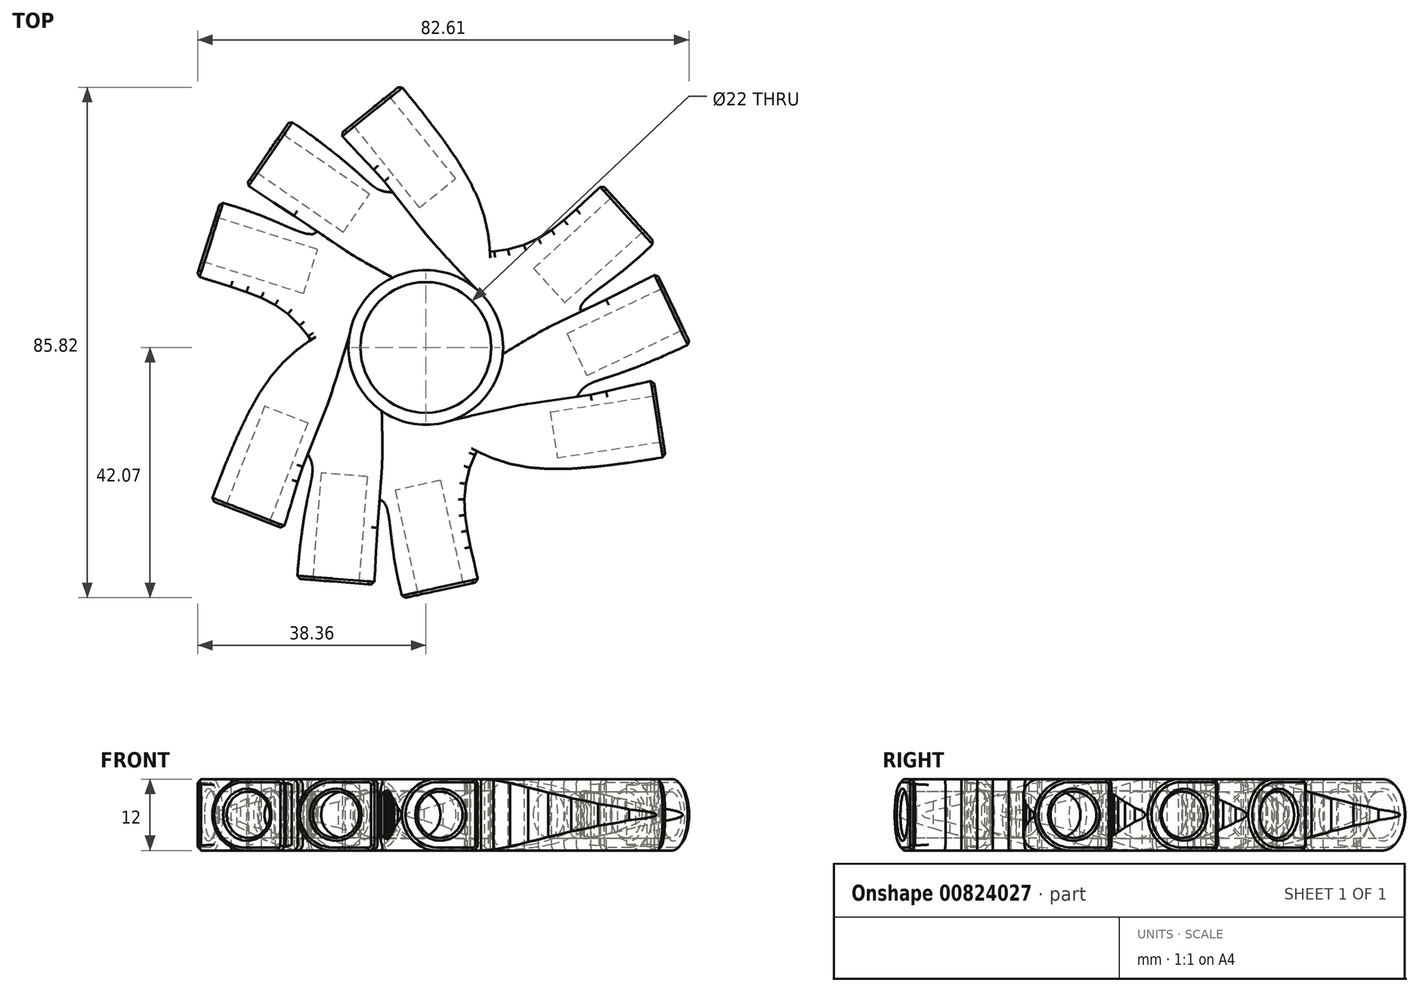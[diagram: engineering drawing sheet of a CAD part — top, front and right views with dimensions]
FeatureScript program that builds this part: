
annotation { "Feature Type Name" : "Feature", "Feature Type Description" : "" }
export const myFeature = defineFeature(function(context is Context, id is Id, definition is map)
    precondition{}
    {
        {
            var Q0;
            Q0=qCreatedBy(makeId("Top.planeOp"),FACE);
            var sketch = newSketch(context, id + "F0", { "sketchPlane" : qUnion([Q0])});
            skLineSegment(sketch, "E0", {"start": v(-3.87, -42.17) * mm, "end": v(8.83, -39.4) * mm});
            skLineSegment(sketch, "E1", {"start": v(8.83, -39.4) * mm, "end": v(8.67, -38.64) * mm});
            skLineSegment(sketch, "E2", {"start": v(8.67, -38.64) * mm, "end": v(8.17, -36.4) * mm});
            skLineSegment(sketch, "E3", {"start": v(8.17, -36.4) * mm, "end": v(7.52, -33.55) * mm});
            skLineSegment(sketch, "E4", {"start": v(7.52, -33.55) * mm, "end": v(6.96, -30.83) * mm});
            skLineSegment(sketch, "E5", {"start": v(6.96, -30.83) * mm, "end": v(6.6, -28.19) * mm});
            skLineSegment(sketch, "E6", {"start": v(6.6, -28.19) * mm, "end": v(6.48, -25.57) * mm});
            skLineSegment(sketch, "E7", {"start": v(6.48, -25.57) * mm, "end": v(6.72, -22.93) * mm});
            skLineSegment(sketch, "E8", {"start": v(6.72, -22.93) * mm, "end": v(7.4, -20.23) * mm});
            skLineSegment(sketch, "E9", {"start": v(7.4, -20.23) * mm, "end": v(8.24, -18.1) * mm});
            skLineSegment(sketch, "E10", {"start": v(8.24, -18.1) * mm, "end": v(8.6, -17.42) * mm});
            skLineSegment(sketch, "E11", {"start": v(8.6, -17.42) * mm, "end": v(9.26, -17.76) * mm});
            skLineSegment(sketch, "E12", {"start": v(9.26, -17.76) * mm, "end": v(11.34, -18.65) * mm});
            skLineSegment(sketch, "E13", {"start": v(11.34, -18.65) * mm, "end": v(14.16, -19.56) * mm});
            skLineSegment(sketch, "E14", {"start": v(14.16, -19.56) * mm, "end": v(17.2, -20.15) * mm});
            skLineSegment(sketch, "E15", {"start": v(17.2, -20.15) * mm, "end": v(20.6, -20.42) * mm});
            skLineSegment(sketch, "E16", {"start": v(20.6, -20.42) * mm, "end": v(24.46, -20.37) * mm});
            skLineSegment(sketch, "E17", {"start": v(24.46, -20.37) * mm, "end": v(28.95, -20.02) * mm});
            skLineSegment(sketch, "E18", {"start": v(28.95, -20.02) * mm, "end": v(34.19, -19.35) * mm});
            skLineSegment(sketch, "E19", {"start": v(34.19, -19.35) * mm, "end": v(38.78, -18.65) * mm});
            skLineSegment(sketch, "E20", {"start": v(38.78, -18.65) * mm, "end": v(40.3, -18.39) * mm});
            skLineSegment(sketch, "E21", {"start": v(40.3, -18.39) * mm, "end": v(38.33, -5.54) * mm});
            skLineSegment(sketch, "E22", {"start": v(38.33, -5.54) * mm, "end": v(37.16, -5.78) * mm});
            skLineSegment(sketch, "E23", {"start": v(37.16, -5.78) * mm, "end": v(33.7, -6.57) * mm});
            skLineSegment(sketch, "E24", {"start": v(33.7, -6.57) * mm, "end": v(30.3, -7.38) * mm});
            skLineSegment(sketch, "E25", {"start": v(30.3, -7.38) * mm, "end": v(27.7, -7.94) * mm});
            skLineSegment(sketch, "E26", {"start": v(27.7, -7.94) * mm, "end": v(26.02, -8.19) * mm});
            skLineSegment(sketch, "E27", {"start": v(26.02, -8.19) * mm, "end": v(25.45, -8.22) * mm});
            skLineSegment(sketch, "E28", {"start": v(25.45, -8.22) * mm, "end": v(25.62, -7.92) * mm});
            skLineSegment(sketch, "E29", {"start": v(25.62, -7.92) * mm, "end": v(26.22, -7.09) * mm});
            skLineSegment(sketch, "E30", {"start": v(26.22, -7.09) * mm, "end": v(27.1, -6.34) * mm});
            skLineSegment(sketch, "E31", {"start": v(27.1, -6.34) * mm, "end": v(28.29, -5.78) * mm});
            skLineSegment(sketch, "E32", {"start": v(28.29, -5.78) * mm, "end": v(29.92, -5.22) * mm});
            skLineSegment(sketch, "E33", {"start": v(29.92, -5.22) * mm, "end": v(32.2, -4.48) * mm});
            skLineSegment(sketch, "E34", {"start": v(32.2, -4.48) * mm, "end": v(35.26, -3.38) * mm});
            skLineSegment(sketch, "E35", {"start": v(35.26, -3.38) * mm, "end": v(39.3, -1.73) * mm});
            skLineSegment(sketch, "E36", {"start": v(39.3, -1.73) * mm, "end": v(43.18, 0.04) * mm});
            skLineSegment(sketch, "E37", {"start": v(43.18, 0.04) * mm, "end": v(44.46, 0.66) * mm});
            skLineSegment(sketch, "E38", {"start": v(44.46, 0.66) * mm, "end": v(38.88, 12.4) * mm});
            skLineSegment(sketch, "E39", {"start": v(38.88, 12.4) * mm, "end": v(37.64, 11.78) * mm});
            skLineSegment(sketch, "E40", {"start": v(37.64, 11.78) * mm, "end": v(33.94, 9.92) * mm});
            skLineSegment(sketch, "E41", {"start": v(33.94, 9.92) * mm, "end": v(30.3, 8.08) * mm});
            skLineSegment(sketch, "E42", {"start": v(30.3, 8.08) * mm, "end": v(27.73, 6.83) * mm});
            skLineSegment(sketch, "E43", {"start": v(27.73, 6.83) * mm, "end": v(26.49, 6.28) * mm});
            skLineSegment(sketch, "E44", {"start": v(26.49, 6.28) * mm, "end": v(26.06, 6.14) * mm});
            skLineSegment(sketch, "E45", {"start": v(26.06, 6.14) * mm, "end": v(25.98, 6.3) * mm});
            skLineSegment(sketch, "E46", {"start": v(25.98, 6.3) * mm, "end": v(26.03, 6.93) * mm});
            skLineSegment(sketch, "E47", {"start": v(26.03, 6.93) * mm, "end": v(26.62, 7.8) * mm});
            skLineSegment(sketch, "E48", {"start": v(26.62, 7.8) * mm, "end": v(27.73, 8.8) * mm});
            skLineSegment(sketch, "E49", {"start": v(27.73, 8.8) * mm, "end": v(29.3, 10) * mm});
            skLineSegment(sketch, "E50", {"start": v(29.3, 10) * mm, "end": v(31.24, 11.44) * mm});
            skLineSegment(sketch, "E51", {"start": v(31.24, 11.44) * mm, "end": v(33.46, 13.17) * mm});
            skLineSegment(sketch, "E52", {"start": v(33.46, 13.17) * mm, "end": v(35.89, 15.24) * mm});
            skLineSegment(sketch, "E53", {"start": v(35.89, 15.24) * mm, "end": v(37.83, 17.06) * mm});
            skLineSegment(sketch, "E54", {"start": v(37.83, 17.06) * mm, "end": v(38.44, 17.7) * mm});
            skLineSegment(sketch, "E55", {"start": v(38.44, 17.7) * mm, "end": v(29.69, 27.3) * mm});
            skLineSegment(sketch, "E56", {"start": v(29.69, 27.3) * mm, "end": v(29.11, 26.8) * mm});
            skLineSegment(sketch, "E57", {"start": v(29.11, 26.8) * mm, "end": v(27.42, 25.23) * mm});
            skLineSegment(sketch, "E58", {"start": v(27.42, 25.23) * mm, "end": v(25.28, 23.25) * mm});
            skLineSegment(sketch, "E59", {"start": v(25.28, 23.25) * mm, "end": v(23.2, 21.41) * mm});
            skLineSegment(sketch, "E60", {"start": v(23.2, 21.41) * mm, "end": v(21.1, 19.77) * mm});
            skLineSegment(sketch, "E61", {"start": v(21.1, 19.77) * mm, "end": v(18.89, 18.37) * mm});
            skLineSegment(sketch, "E62", {"start": v(18.89, 18.37) * mm, "end": v(16.48, 17.26) * mm});
            skLineSegment(sketch, "E63", {"start": v(16.48, 17.26) * mm, "end": v(13.8, 16.5) * mm});
            skLineSegment(sketch, "E64", {"start": v(13.8, 16.5) * mm, "end": v(11.53, 16.15) * mm});
            skLineSegment(sketch, "E65", {"start": v(11.53, 16.15) * mm, "end": v(10.77, 16.12) * mm});
            skLineSegment(sketch, "E66", {"start": v(10.77, 16.12) * mm, "end": v(10.73, 16.87) * mm});
            skLineSegment(sketch, "E67", {"start": v(10.73, 16.87) * mm, "end": v(10.47, 19.11) * mm});
            skLineSegment(sketch, "E68", {"start": v(10.47, 19.11) * mm, "end": v(9.84, 22.01) * mm});
            skLineSegment(sketch, "E69", {"start": v(9.84, 22.01) * mm, "end": v(8.83, 24.94) * mm});
            skLineSegment(sketch, "E70", {"start": v(8.83, 24.94) * mm, "end": v(7.37, 28) * mm});
            skLineSegment(sketch, "E71", {"start": v(7.37, 28) * mm, "end": v(5.4, 31.34) * mm});
            skLineSegment(sketch, "E72", {"start": v(5.4, 31.34) * mm, "end": v(2.84, 35.05) * mm});
            skLineSegment(sketch, "E73", {"start": v(2.84, 35.05) * mm, "end": v(-0.35, 39.25) * mm});
            skLineSegment(sketch, "E74", {"start": v(-0.35, 39.25) * mm, "end": v(-3.26, 42.87) * mm});
            skLineSegment(sketch, "E75", {"start": v(-3.26, 42.87) * mm, "end": v(-4.24, 44.06) * mm});
            skLineSegment(sketch, "E76", {"start": v(-4.24, 44.06) * mm, "end": v(-14.38, 35.92) * mm});
            skLineSegment(sketch, "E77", {"start": v(-14.38, 35.92) * mm, "end": v(-13.6, 35.04) * mm});
            skLineSegment(sketch, "E78", {"start": v(-13.6, 35.04) * mm, "end": v(-11.17, 32.43) * mm});
            skLineSegment(sketch, "E79", {"start": v(-11.17, 32.43) * mm, "end": v(-8.77, 29.9) * mm});
            skLineSegment(sketch, "E80", {"start": v(-8.77, 29.9) * mm, "end": v(-7, 27.93) * mm});
            skLineSegment(sketch, "E81", {"start": v(-7, 27.93) * mm, "end": v(-5.94, 26.59) * mm});
            skLineSegment(sketch, "E82", {"start": v(-5.94, 26.59) * mm, "end": v(-5.63, 26.11) * mm});
            skLineSegment(sketch, "E83", {"start": v(-5.63, 26.11) * mm, "end": v(-5.97, 26.1) * mm});
            skLineSegment(sketch, "E84", {"start": v(-5.97, 26.1) * mm, "end": v(-6.99, 26.21) * mm});
            skLineSegment(sketch, "E85", {"start": v(-6.99, 26.21) * mm, "end": v(-8.08, 26.6) * mm});
            skLineSegment(sketch, "E86", {"start": v(-8.08, 26.6) * mm, "end": v(-9.16, 27.35) * mm});
            skLineSegment(sketch, "E87", {"start": v(-9.16, 27.35) * mm, "end": v(-10.46, 28.5) * mm});
            skLineSegment(sketch, "E88", {"start": v(-10.46, 28.5) * mm, "end": v(-12.23, 30.09) * mm});
            skLineSegment(sketch, "E89", {"start": v(-12.23, 30.09) * mm, "end": v(-14.72, 32.2) * mm});
            skLineSegment(sketch, "E90", {"start": v(-14.72, 32.2) * mm, "end": v(-18.17, 34.86) * mm});
            skLineSegment(sketch, "E91", {"start": v(-18.17, 34.86) * mm, "end": v(-21.64, 37.35) * mm});
            skLineSegment(sketch, "E92", {"start": v(-21.64, 37.35) * mm, "end": v(-22.82, 38.14) * mm});
            skLineSegment(sketch, "E93", {"start": v(-22.82, 38.14) * mm, "end": v(-30.2, 27.43) * mm});
            skLineSegment(sketch, "E94", {"start": v(-30.2, 27.43) * mm, "end": v(-29.04, 26.67) * mm});
            skLineSegment(sketch, "E95", {"start": v(-29.04, 26.67) * mm, "end": v(-25.58, 24.4) * mm});
            skLineSegment(sketch, "E96", {"start": v(-25.58, 24.4) * mm, "end": v(-22.16, 22.16) * mm});
            skLineSegment(sketch, "E97", {"start": v(-22.16, 22.16) * mm, "end": v(-19.8, 20.56) * mm});
            skLineSegment(sketch, "E98", {"start": v(-19.8, 20.56) * mm, "end": v(-18.7, 19.76) * mm});
            skLineSegment(sketch, "E99", {"start": v(-18.7, 19.76) * mm, "end": v(-18.36, 19.46) * mm});
            skLineSegment(sketch, "E100", {"start": v(-18.36, 19.46) * mm, "end": v(-18.46, 19.31) * mm});
            skLineSegment(sketch, "E101", {"start": v(-18.46, 19.31) * mm, "end": v(-19.03, 19.04) * mm});
            skLineSegment(sketch, "E102", {"start": v(-19.03, 19.04) * mm, "end": v(-20.08, 19.11) * mm});
            skLineSegment(sketch, "E103", {"start": v(-20.08, 19.11) * mm, "end": v(-21.51, 19.58) * mm});
            skLineSegment(sketch, "E104", {"start": v(-21.51, 19.58) * mm, "end": v(-23.33, 20.34) * mm});
            skLineSegment(sketch, "E105", {"start": v(-23.33, 20.34) * mm, "end": v(-25.54, 21.3) * mm});
            skLineSegment(sketch, "E106", {"start": v(-25.54, 21.3) * mm, "end": v(-28.15, 22.36) * mm});
            skLineSegment(sketch, "E107", {"start": v(-28.15, 22.36) * mm, "end": v(-31.16, 23.43) * mm});
            skLineSegment(sketch, "E108", {"start": v(-31.16, 23.43) * mm, "end": v(-33.7, 24.2) * mm});
            skLineSegment(sketch, "E109", {"start": v(-33.7, 24.2) * mm, "end": v(-34.56, 24.4) * mm});
            skLineSegment(sketch, "E110", {"start": v(-34.56, 24.4) * mm, "end": v(-38.5, 12.02) * mm});
            skLineSegment(sketch, "E111", {"start": v(-38.5, 12.02) * mm, "end": v(-37.78, 11.78) * mm});
            skLineSegment(sketch, "E112", {"start": v(-37.78, 11.78) * mm, "end": v(-35.58, 11.1) * mm});
            skLineSegment(sketch, "E113", {"start": v(-35.58, 11.1) * mm, "end": v(-32.8, 10.23) * mm});
            skLineSegment(sketch, "E114", {"start": v(-32.8, 10.23) * mm, "end": v(-30.16, 9.35) * mm});
            skLineSegment(sketch, "E115", {"start": v(-30.16, 9.35) * mm, "end": v(-27.69, 8.35) * mm});
            skLineSegment(sketch, "E116", {"start": v(-27.69, 8.35) * mm, "end": v(-25.36, 7.14) * mm});
            skLineSegment(sketch, "E117", {"start": v(-25.36, 7.14) * mm, "end": v(-23.2, 5.61) * mm});
            skLineSegment(sketch, "E118", {"start": v(-23.2, 5.61) * mm, "end": v(-21.2, 3.68) * mm});
            skLineSegment(sketch, "E119", {"start": v(-21.2, 3.68) * mm, "end": v(-19.77, 1.88) * mm});
            skLineSegment(sketch, "E120", {"start": v(-19.77, 1.88) * mm, "end": v(-19.36, 1.24) * mm});
            skLineSegment(sketch, "E121", {"start": v(-19.36, 1.24) * mm, "end": v(-20, 0.83) * mm});
            skLineSegment(sketch, "E122", {"start": v(-20, 0.83) * mm, "end": v(-21.8, -0.52) * mm});
            skLineSegment(sketch, "E123", {"start": v(-21.8, -0.52) * mm, "end": v(-24, -2.52) * mm});
            skLineSegment(sketch, "E124", {"start": v(-24, -2.52) * mm, "end": v(-26.03, -4.86) * mm});
            skLineSegment(sketch, "E125", {"start": v(-26.03, -4.86) * mm, "end": v(-27.96, -7.66) * mm});
            skLineSegment(sketch, "E126", {"start": v(-27.96, -7.66) * mm, "end": v(-29.85, -11.03) * mm});
            skLineSegment(sketch, "E127", {"start": v(-29.85, -11.03) * mm, "end": v(-31.79, -15.1) * mm});
            skLineSegment(sketch, "E128", {"start": v(-31.79, -15.1) * mm, "end": v(-33.83, -19.96) * mm});
            skLineSegment(sketch, "E129", {"start": v(-33.83, -19.96) * mm, "end": v(-35.51, -24.3) * mm});
            skLineSegment(sketch, "E130", {"start": v(-35.51, -24.3) * mm, "end": v(-36.05, -25.74) * mm});
            skLineSegment(sketch, "E131", {"start": v(-36.05, -25.74) * mm, "end": v(-23.94, -30.45) * mm});
            skLineSegment(sketch, "E132", {"start": v(-23.94, -30.45) * mm, "end": v(-23.57, -29.33) * mm});
            skLineSegment(sketch, "E133", {"start": v(-23.57, -29.33) * mm, "end": v(-22.52, -25.92) * mm});
            skLineSegment(sketch, "E134", {"start": v(-22.52, -25.92) * mm, "end": v(-21.52, -22.58) * mm});
            skLineSegment(sketch, "E135", {"start": v(-21.52, -22.58) * mm, "end": v(-20.7, -20.06) * mm});
            skLineSegment(sketch, "E136", {"start": v(-20.7, -20.06) * mm, "end": v(-20.07, -18.47) * mm});
            skLineSegment(sketch, "E137", {"start": v(-20.07, -18.47) * mm, "end": v(-19.82, -17.97) * mm});
            skLineSegment(sketch, "E138", {"start": v(-19.82, -17.97) * mm, "end": v(-19.64, -18.26) * mm});
            skLineSegment(sketch, "E139", {"start": v(-19.64, -18.26) * mm, "end": v(-19.23, -19.2) * mm});
            skLineSegment(sketch, "E140", {"start": v(-19.23, -19.2) * mm, "end": v(-19.02, -20.34) * mm});
            skLineSegment(sketch, "E141", {"start": v(-19.02, -20.34) * mm, "end": v(-19.12, -21.64) * mm});
            skLineSegment(sketch, "E142", {"start": v(-19.12, -21.64) * mm, "end": v(-19.46, -23.34) * mm});
            skLineSegment(sketch, "E143", {"start": v(-19.46, -23.34) * mm, "end": v(-19.96, -25.67) * mm});
            skLineSegment(sketch, "E144", {"start": v(-19.96, -25.67) * mm, "end": v(-20.53, -28.88) * mm});
            skLineSegment(sketch, "E145", {"start": v(-20.53, -28.88) * mm, "end": v(-21.12, -33.2) * mm});
            skLineSegment(sketch, "E146", {"start": v(-21.12, -33.2) * mm, "end": v(-21.54, -37.45) * mm});
            skLineSegment(sketch, "E147", {"start": v(-21.54, -37.45) * mm, "end": v(-21.64, -38.87) * mm});
            skLineSegment(sketch, "E148", {"start": v(-21.64, -38.87) * mm, "end": v(-8.68, -39.9) * mm});
            skLineSegment(sketch, "E149", {"start": v(-8.68, -39.9) * mm, "end": v(-8.6, -38.52) * mm});
            skLineSegment(sketch, "E150", {"start": v(-8.6, -38.52) * mm, "end": v(-8.36, -34.39) * mm});
            skLineSegment(sketch, "E151", {"start": v(-8.36, -34.39) * mm, "end": v(-8.13, -30.3) * mm});
            skLineSegment(sketch, "E152", {"start": v(-8.13, -30.3) * mm, "end": v(-7.92, -27.46) * mm});
            skLineSegment(sketch, "E153", {"start": v(-7.92, -27.46) * mm, "end": v(-7.78, -26.11) * mm});
            skLineSegment(sketch, "E154", {"start": v(-7.78, -26.11) * mm, "end": v(-7.69, -25.67) * mm});
            skLineSegment(sketch, "E155", {"start": v(-7.69, -25.67) * mm, "end": v(-7.51, -25.68) * mm});
            skLineSegment(sketch, "E156", {"start": v(-7.51, -25.68) * mm, "end": v(-7, -26.04) * mm});
            skLineSegment(sketch, "E157", {"start": v(-7, -26.04) * mm, "end": v(-6.53, -26.98) * mm});
            skLineSegment(sketch, "E158", {"start": v(-6.53, -26.98) * mm, "end": v(-6.22, -28.45) * mm});
            skLineSegment(sketch, "E159", {"start": v(-6.22, -28.45) * mm, "end": v(-5.96, -30.41) * mm});
            skLineSegment(sketch, "E160", {"start": v(-5.96, -30.41) * mm, "end": v(-5.69, -32.8) * mm});
            skLineSegment(sketch, "E161", {"start": v(-5.69, -32.8) * mm, "end": v(-5.3, -35.6) * mm});
            skLineSegment(sketch, "E162", {"start": v(-5.3, -35.6) * mm, "end": v(-4.73, -38.73) * mm});
            skLineSegment(sketch, "E163", {"start": v(-4.73, -38.73) * mm, "end": v(-4.12, -41.32) * mm});
            skLineSegment(sketch, "E164", {"start": v(-4.12, -41.32) * mm, "end": v(-3.87, -42.17) * mm});
            skCircle(sketch, "E165", {"center": v(0, 0) * mm, "radius": 11 * mm});
            skSolve(sketch);
        }
        {
            var Q0;
            Q0=makeQuery(id+"F0.imprint","IMPRINT",FACE,{"disambiguationData":[TD([[makeQuery(id+"F0.imprint","IMPRINT",EDGE,{"derivedFrom":sQuery(id+"F0.wireOp",EDGE,"E0")}),1.0]])]});
            extrude(context, id + "F1", {"entities" : qUnion([Q0]), "endBound" : BoundingType.SYMMETRIC, "depth" : 12 * mm, "offsetDistance" : 25 * mm});
        }
        {
            var Q0;
            Q0=makeQuery(id+"F1.opExtrude","CAP_EDGE",EDGE,{"disambiguationData":[OSD([sQuery(id+"F0.wireOp",EDGE,"E130")])],"isStart":false});
            var Q1;
            Q1=makeQuery(id+"F1.opExtrude","CAP_EDGE",EDGE,{"disambiguationData":[OSD([sQuery(id+"F0.wireOp",EDGE,"E147")])],"isStart":false});
            var Q2;
            Q2=makeQuery(id+"F1.opExtrude","CAP_EDGE",EDGE,{"disambiguationData":[OSD([sQuery(id+"F0.wireOp",EDGE,"E164")])],"isStart":false});
            var Q3;
            Q3=makeQuery(id+"F1.opExtrude","CAP_EDGE",EDGE,{"disambiguationData":[OSD([sQuery(id+"F0.wireOp",EDGE,"E20")])],"isStart":false});
            var Q4;
            Q4=makeQuery(id+"F1.opExtrude","CAP_EDGE",EDGE,{"disambiguationData":[OSD([sQuery(id+"F0.wireOp",EDGE,"E37")])],"isStart":false});
            var Q5;
            Q5=makeQuery(id+"F1.opExtrude","CAP_EDGE",EDGE,{"disambiguationData":[OSD([sQuery(id+"F0.wireOp",EDGE,"E54")])],"isStart":false});
            var Q6;
            Q6=makeQuery(id+"F1.opExtrude","CAP_EDGE",EDGE,{"disambiguationData":[OSD([sQuery(id+"F0.wireOp",EDGE,"E75")])],"isStart":false});
            var Q7;
            Q7=makeQuery(id+"F1.opExtrude","CAP_EDGE",EDGE,{"disambiguationData":[OSD([sQuery(id+"F0.wireOp",EDGE,"E92")])],"isStart":false});
            var Q8;
            Q8=makeQuery(id+"F1.opExtrude","CAP_EDGE",EDGE,{"disambiguationData":[OSD([sQuery(id+"F0.wireOp",EDGE,"E109")])],"isStart":false});
            fillet(context, id + "F2", {"entities" : qUnion([Q0, Q1, Q2, Q3, Q4, Q5, Q6, Q7, Q8]), "radius" : 6 * mm, "tangentPropagation" : true, "allowEdgeOverflow" : false});
        }
        {
            var Q0;
            Q0=makeQuery(id+"F1.opExtrude","CAP_EDGE",EDGE,{"disambiguationData":[OSD([sQuery(id+"F0.wireOp",EDGE,"E147")])],"isStart":true});
            var Q1;
            Q1=makeQuery(id+"F1.opExtrude","CAP_EDGE",EDGE,{"disambiguationData":[OSD([sQuery(id+"F0.wireOp",EDGE,"E130")])],"isStart":true});
            var Q2;
            Q2=makeQuery(id+"F1.opExtrude","CAP_EDGE",EDGE,{"disambiguationData":[OSD([sQuery(id+"F0.wireOp",EDGE,"E164")])],"isStart":true});
            var Q3;
            Q3=makeQuery(id+"F1.opExtrude","CAP_EDGE",EDGE,{"disambiguationData":[OSD([sQuery(id+"F0.wireOp",EDGE,"E20")])],"isStart":true});
            var Q4;
            Q4=makeQuery(id+"F1.opExtrude","CAP_EDGE",EDGE,{"disambiguationData":[OSD([sQuery(id+"F0.wireOp",EDGE,"E37")])],"isStart":true});
            var Q5;
            Q5=makeQuery(id+"F1.opExtrude","CAP_EDGE",EDGE,{"disambiguationData":[OSD([sQuery(id+"F0.wireOp",EDGE,"E54")])],"isStart":true});
            var Q6;
            Q6=makeQuery(id+"F1.opExtrude","CAP_EDGE",EDGE,{"disambiguationData":[OSD([sQuery(id+"F0.wireOp",EDGE,"E75")])],"isStart":true});
            var Q7;
            Q7=makeQuery(id+"F1.opExtrude","CAP_EDGE",EDGE,{"disambiguationData":[OSD([sQuery(id+"F0.wireOp",EDGE,"E92")])],"isStart":true});
            var Q8;
            Q8=makeQuery(id+"F1.opExtrude","CAP_EDGE",EDGE,{"disambiguationData":[OSD([sQuery(id+"F0.wireOp",EDGE,"E109")])],"isStart":true});
            fillet(context, id + "F3", {"entities" : qUnion([Q0, Q1, Q2, Q3, Q4, Q5, Q6, Q7, Q8]), "radius" : 6 * mm, "tangentPropagation" : true, "allowEdgeOverflow" : false});
        }
        {
            var Q0;
            Q0=makeQuery(id+"F1.opExtrude","CAP_EDGE",EDGE,{"disambiguationData":[OSD([sQuery(id+"F0.wireOp",EDGE,"E165")])],"isStart":false});
            chamfer(context, id + "F4", {"entities" : qUnion([Q0]), "width" : 2 * mm, "tangentPropagation" : true});
        }
        {
            var Q0;
            Q0=makeQuery(id+"F1.opExtrude","CAP_EDGE",EDGE,{"disambiguationData":[OSD([sQuery(id+"F0.wireOp",EDGE,"E165")])],"isStart":true});
            chamfer(context, id + "F5", {"entities" : qUnion([Q0]), "width" : 2 * mm, "tangentPropagation" : true});
        }
        {
            var Q0;
            Q0=makeQuery(id+"F1.opExtrude","CAP_EDGE",EDGE,{"disambiguationData":[OSD([sQuery(id+"F0.wireOp",EDGE,"E136")])],"isStart":false});
            var Q1;
            Q1=makeQuery(id+"F1.opExtrude","CAP_EDGE",EDGE,{"disambiguationData":[OSD([sQuery(id+"F0.wireOp",EDGE,"E135")])],"isStart":false});
            var Q2;
            Q2=makeQuery(id+"F1.opExtrude","CAP_EDGE",EDGE,{"disambiguationData":[OSD([sQuery(id+"F0.wireOp",EDGE,"E152")])],"isStart":false});
            var Q3;
            Q3=makeQuery(id+"F1.opExtrude","CAP_EDGE",EDGE,{"disambiguationData":[OSD([sQuery(id+"F0.wireOp",EDGE,"E10")])],"isStart":false});
            var Q4;
            Q4=makeQuery(id+"F1.opExtrude","CAP_EDGE",EDGE,{"disambiguationData":[OSD([sQuery(id+"F0.wireOp",EDGE,"E8")])],"isStart":false});
            var Q5;
            Q5=makeQuery(id+"F1.opExtrude","CAP_EDGE",EDGE,{"disambiguationData":[OSD([sQuery(id+"F0.wireOp",EDGE,"E9")])],"isStart":false});
            var Q6;
            Q6=makeQuery(id+"F1.opExtrude","CAP_EDGE",EDGE,{"disambiguationData":[OSD([sQuery(id+"F0.wireOp",EDGE,"E7")])],"isStart":false});
            var Q7;
            Q7=makeQuery(id+"F1.opExtrude","CAP_EDGE",EDGE,{"disambiguationData":[OSD([sQuery(id+"F0.wireOp",EDGE,"E6")])],"isStart":false});
            var Q8;
            Q8=makeQuery(id+"F1.opExtrude","CAP_EDGE",EDGE,{"disambiguationData":[OSD([sQuery(id+"F0.wireOp",EDGE,"E5")])],"isStart":false});
            var Q9;
            Q9=makeQuery(id+"F1.opExtrude","CAP_EDGE",EDGE,{"disambiguationData":[OSD([sQuery(id+"F0.wireOp",EDGE,"E4")])],"isStart":false});
            var Q10;
            Q10=makeQuery(id+"F1.opExtrude","CAP_EDGE",EDGE,{"disambiguationData":[OSD([sQuery(id+"F0.wireOp",EDGE,"E26")])],"isStart":false});
            var Q11;
            Q11=makeQuery(id+"F1.opExtrude","CAP_EDGE",EDGE,{"disambiguationData":[OSD([sQuery(id+"F0.wireOp",EDGE,"E25")])],"isStart":false});
            var Q12;
            Q12=makeQuery(id+"F1.opExtrude","CAP_EDGE",EDGE,{"disambiguationData":[OSD([sQuery(id+"F0.wireOp",EDGE,"E42")])],"isStart":false});
            var Q13;
            Q13=makeQuery(id+"F1.opExtrude","CAP_EDGE",EDGE,{"disambiguationData":[OSD([sQuery(id+"F0.wireOp",EDGE,"E65")])],"isStart":false});
            var Q14;
            Q14=makeQuery(id+"F1.opExtrude","CAP_EDGE",EDGE,{"disambiguationData":[OSD([sQuery(id+"F0.wireOp",EDGE,"E64")])],"isStart":false});
            var Q15;
            Q15=makeQuery(id+"F1.opExtrude","CAP_EDGE",EDGE,{"disambiguationData":[OSD([sQuery(id+"F0.wireOp",EDGE,"E63")])],"isStart":false});
            var Q16;
            Q16=makeQuery(id+"F1.opExtrude","CAP_EDGE",EDGE,{"disambiguationData":[OSD([sQuery(id+"F0.wireOp",EDGE,"E62")])],"isStart":false});
            var Q17;
            Q17=makeQuery(id+"F1.opExtrude","CAP_EDGE",EDGE,{"disambiguationData":[OSD([sQuery(id+"F0.wireOp",EDGE,"E61")])],"isStart":false});
            var Q18;
            Q18=makeQuery(id+"F1.opExtrude","CAP_EDGE",EDGE,{"disambiguationData":[OSD([sQuery(id+"F0.wireOp",EDGE,"E60")])],"isStart":false});
            var Q19;
            Q19=makeQuery(id+"F1.opExtrude","CAP_EDGE",EDGE,{"disambiguationData":[OSD([sQuery(id+"F0.wireOp",EDGE,"E81")])],"isStart":false});
            var Q20;
            Q20=makeQuery(id+"F1.opExtrude","CAP_EDGE",EDGE,{"disambiguationData":[OSD([sQuery(id+"F0.wireOp",EDGE,"E97")])],"isStart":false});
            var Q21;
            Q21=makeQuery(id+"F1.opExtrude","CAP_EDGE",EDGE,{"disambiguationData":[OSD([sQuery(id+"F0.wireOp",EDGE,"E80")])],"isStart":false});
            var Q22;
            Q22=makeQuery(id+"F1.opExtrude","CAP_EDGE",EDGE,{"disambiguationData":[OSD([sQuery(id+"F0.wireOp",EDGE,"E120")])],"isStart":false});
            var Q23;
            Q23=makeQuery(id+"F1.opExtrude","CAP_EDGE",EDGE,{"disambiguationData":[OSD([sQuery(id+"F0.wireOp",EDGE,"E119")])],"isStart":false});
            var Q24;
            Q24=makeQuery(id+"F1.opExtrude","CAP_EDGE",EDGE,{"disambiguationData":[OSD([sQuery(id+"F0.wireOp",EDGE,"E118")])],"isStart":false});
            var Q25;
            Q25=makeQuery(id+"F1.opExtrude","CAP_EDGE",EDGE,{"disambiguationData":[OSD([sQuery(id+"F0.wireOp",EDGE,"E117")])],"isStart":false});
            var Q26;
            Q26=makeQuery(id+"F1.opExtrude","CAP_EDGE",EDGE,{"disambiguationData":[OSD([sQuery(id+"F0.wireOp",EDGE,"E116")])],"isStart":false});
            var Q27;
            Q27=makeQuery(id+"F1.opExtrude","CAP_EDGE",EDGE,{"disambiguationData":[OSD([sQuery(id+"F0.wireOp",EDGE,"E115")])],"isStart":false});
            var Q28;
            Q28=makeQuery(id+"F1.opExtrude","CAP_EDGE",EDGE,{"disambiguationData":[OSD([sQuery(id+"F0.wireOp",EDGE,"E114")])],"isStart":false});
            var Q29;
            Q29=makeQuery(id+"F1.opExtrude","CAP_EDGE",EDGE,{"disambiguationData":[OSD([sQuery(id+"F0.wireOp",EDGE,"E136")])],"isStart":true});
            var Q30;
            Q30=makeQuery(id+"F1.opExtrude","CAP_EDGE",EDGE,{"disambiguationData":[OSD([sQuery(id+"F0.wireOp",EDGE,"E135")])],"isStart":true});
            var Q31;
            Q31=makeQuery(id+"F1.opExtrude","CAP_EDGE",EDGE,{"disambiguationData":[OSD([sQuery(id+"F0.wireOp",EDGE,"E152")])],"isStart":true});
            var Q32;
            Q32=makeQuery(id+"F1.opExtrude","CAP_EDGE",EDGE,{"disambiguationData":[OSD([sQuery(id+"F0.wireOp",EDGE,"E10")])],"isStart":true});
            var Q33;
            Q33=makeQuery(id+"F1.opExtrude","CAP_EDGE",EDGE,{"disambiguationData":[OSD([sQuery(id+"F0.wireOp",EDGE,"E9")])],"isStart":true});
            var Q34;
            Q34=makeQuery(id+"F1.opExtrude","CAP_EDGE",EDGE,{"disambiguationData":[OSD([sQuery(id+"F0.wireOp",EDGE,"E8")])],"isStart":true});
            var Q35;
            Q35=makeQuery(id+"F1.opExtrude","CAP_EDGE",EDGE,{"disambiguationData":[OSD([sQuery(id+"F0.wireOp",EDGE,"E7")])],"isStart":true});
            var Q36;
            Q36=makeQuery(id+"F1.opExtrude","CAP_EDGE",EDGE,{"disambiguationData":[OSD([sQuery(id+"F0.wireOp",EDGE,"E6")])],"isStart":true});
            var Q37;
            Q37=makeQuery(id+"F1.opExtrude","CAP_EDGE",EDGE,{"disambiguationData":[OSD([sQuery(id+"F0.wireOp",EDGE,"E5")])],"isStart":true});
            var Q38;
            Q38=makeQuery(id+"F1.opExtrude","CAP_EDGE",EDGE,{"disambiguationData":[OSD([sQuery(id+"F0.wireOp",EDGE,"E4")])],"isStart":true});
            var Q39;
            Q39=makeQuery(id+"F1.opExtrude","CAP_EDGE",EDGE,{"disambiguationData":[OSD([sQuery(id+"F0.wireOp",EDGE,"E26")])],"isStart":true});
            var Q40;
            Q40=makeQuery(id+"F1.opExtrude","CAP_EDGE",EDGE,{"disambiguationData":[OSD([sQuery(id+"F0.wireOp",EDGE,"E25")])],"isStart":true});
            var Q41;
            Q41=makeQuery(id+"F1.opExtrude","CAP_EDGE",EDGE,{"disambiguationData":[OSD([sQuery(id+"F0.wireOp",EDGE,"E42")])],"isStart":true});
            var Q42;
            Q42=makeQuery(id+"F1.opExtrude","CAP_EDGE",EDGE,{"disambiguationData":[OSD([sQuery(id+"F0.wireOp",EDGE,"E65")])],"isStart":true});
            var Q43;
            Q43=makeQuery(id+"F1.opExtrude","CAP_EDGE",EDGE,{"disambiguationData":[OSD([sQuery(id+"F0.wireOp",EDGE,"E64")])],"isStart":true});
            var Q44;
            Q44=makeQuery(id+"F1.opExtrude","CAP_EDGE",EDGE,{"disambiguationData":[OSD([sQuery(id+"F0.wireOp",EDGE,"E63")])],"isStart":true});
            var Q45;
            Q45=makeQuery(id+"F1.opExtrude","CAP_EDGE",EDGE,{"disambiguationData":[OSD([sQuery(id+"F0.wireOp",EDGE,"E62")])],"isStart":true});
            var Q46;
            Q46=makeQuery(id+"F1.opExtrude","CAP_EDGE",EDGE,{"disambiguationData":[OSD([sQuery(id+"F0.wireOp",EDGE,"E61")])],"isStart":true});
            var Q47;
            Q47=makeQuery(id+"F1.opExtrude","CAP_EDGE",EDGE,{"disambiguationData":[OSD([sQuery(id+"F0.wireOp",EDGE,"E60")])],"isStart":true});
            var Q48;
            Q48=makeQuery(id+"F1.opExtrude","CAP_EDGE",EDGE,{"disambiguationData":[OSD([sQuery(id+"F0.wireOp",EDGE,"E81")])],"isStart":true});
            var Q49;
            Q49=makeQuery(id+"F1.opExtrude","CAP_EDGE",EDGE,{"disambiguationData":[OSD([sQuery(id+"F0.wireOp",EDGE,"E80")])],"isStart":true});
            var Q50;
            Q50=makeQuery(id+"F1.opExtrude","CAP_EDGE",EDGE,{"disambiguationData":[OSD([sQuery(id+"F0.wireOp",EDGE,"E97")])],"isStart":true});
            var Q51;
            Q51=makeQuery(id+"F1.opExtrude","CAP_EDGE",EDGE,{"disambiguationData":[OSD([sQuery(id+"F0.wireOp",EDGE,"E120")])],"isStart":true});
            var Q52;
            Q52=makeQuery(id+"F1.opExtrude","CAP_EDGE",EDGE,{"disambiguationData":[OSD([sQuery(id+"F0.wireOp",EDGE,"E119")])],"isStart":true});
            var Q53;
            Q53=makeQuery(id+"F1.opExtrude","CAP_EDGE",EDGE,{"disambiguationData":[OSD([sQuery(id+"F0.wireOp",EDGE,"E118")])],"isStart":true});
            var Q54;
            Q54=makeQuery(id+"F1.opExtrude","CAP_EDGE",EDGE,{"disambiguationData":[OSD([sQuery(id+"F0.wireOp",EDGE,"E117")])],"isStart":true});
            var Q55;
            Q55=makeQuery(id+"F1.opExtrude","CAP_EDGE",EDGE,{"disambiguationData":[OSD([sQuery(id+"F0.wireOp",EDGE,"E116")])],"isStart":true});
            var Q56;
            Q56=makeQuery(id+"F1.opExtrude","CAP_EDGE",EDGE,{"disambiguationData":[OSD([sQuery(id+"F0.wireOp",EDGE,"E115")])],"isStart":true});
            var Q57;
            Q57=makeQuery(id+"F1.opExtrude","CAP_EDGE",EDGE,{"disambiguationData":[OSD([sQuery(id+"F0.wireOp",EDGE,"E114")])],"isStart":true});
            fillet(context, id + "F6", {"entities" : qUnion([Q0, Q1, Q2, Q3, Q4, Q5, Q6, Q7, Q8, Q9, Q10, Q11, Q12, Q13, Q14, Q15, Q16, Q17, Q18, Q19, Q20, Q21, Q22, Q23, Q24, Q25, Q26, Q27, Q28, Q29, Q30, Q31, Q32, Q33, Q34, Q35, Q36, Q37, Q38, Q39, Q40, Q41, Q42, Q43, Q44, Q45, Q46, Q47, Q48, Q49, Q50, Q51, Q52, Q53, Q54, Q55, Q56, Q57]), "radius" : 1 * mm, "tangentPropagation" : true, "allowEdgeOverflow" : false});
        }
        {
            var Q0;
            Q0=makeQuery(id+"F1.opExtrude","SWEPT_FACE",FACE,{"disambiguationData":[OSD([sQuery(id+"F0.wireOp",EDGE,"E148")])]});
            var Q1;
            Q1=makeQuery(id+"F1.opExtrude","SWEPT_FACE",FACE,{"disambiguationData":[OSD([sQuery(id+"F0.wireOp",EDGE,"E131")])]});
            var Q2;
            Q2=makeQuery(id+"F1.opExtrude","SWEPT_FACE",FACE,{"disambiguationData":[OSD([sQuery(id+"F0.wireOp",EDGE,"E0")])]});
            var Q3;
            Q3=makeQuery(id+"F1.opExtrude","SWEPT_FACE",FACE,{"disambiguationData":[OSD([sQuery(id+"F0.wireOp",EDGE,"E110")])]});
            var Q4;
            Q4=makeQuery(id+"F1.opExtrude","SWEPT_FACE",FACE,{"disambiguationData":[OSD([sQuery(id+"F0.wireOp",EDGE,"E93")])]});
            var Q5;
            Q5=makeQuery(id+"F1.opExtrude","SWEPT_FACE",FACE,{"disambiguationData":[OSD([sQuery(id+"F0.wireOp",EDGE,"E76")])]});
            var Q6;
            Q6=makeQuery(id+"F1.opExtrude","SWEPT_FACE",FACE,{"disambiguationData":[OSD([sQuery(id+"F0.wireOp",EDGE,"E55")])]});
            var Q7;
            Q7=makeQuery(id+"F1.opExtrude","SWEPT_FACE",FACE,{"disambiguationData":[OSD([sQuery(id+"F0.wireOp",EDGE,"E38")])]});
            var Q8;
            Q8=makeQuery(id+"F1.opExtrude","SWEPT_FACE",FACE,{"disambiguationData":[OSD([sQuery(id+"F0.wireOp",EDGE,"E21")])]});
            chamfer(context, id + "F7", {"entities" : qUnion([Q0, Q1, Q2, Q3, Q4, Q5, Q6, Q7, Q8]), "width" : 0.5 * mm, "tangentPropagation" : true});
        }
        {
            var Q0;
            Q0=makeQuery(id+"F1.opExtrude","SWEPT_FACE",FACE,{"disambiguationData":[OSD([sQuery(id+"F0.wireOp",EDGE,"E76")])]});
            var sketch = newSketch(context, id + "F8", { "sketchPlane" : qUnion([Q0])});
            skLineSegment(sketch, "E166", {"start": v(-23.77, 0) * mm, "end": v(-11.8, 0) * mm, "construction": true});
            skCircle(sketch, "E167", {"center": v(-17.79, 0) * mm, "radius": 3.9 * mm});
            skSolve(sketch);
        }
        {
            var Q0;
            Q0=makeQuery(id+"F8.imprint","IMPRINT",FACE,{"disambiguationData":[TD([[makeQuery(id+"F8.imprint","IMPRINT",EDGE,{"derivedFrom":sQuery(id+"F8.wireOp",EDGE,"E167")}),1.0]])]});
            extrude(context, id + "F9", {"entities" : qUnion([Q0]), "oppositeDirection" : true, "depth" : 18 * mm, "offsetDistance" : 25 * mm, "hasSecondDirection" : true, "secondDirectionOppositeDirection" : false, "secondDirectionDepth" : 1 * mm});
        }
        {
            var Q0;
            Q0=qCreatedBy(makeId("Front.planeOp"),FACE);
            var sketch = newSketch(context, id + "F10", { "sketchPlane" : qUnion([Q0])});
            skLineSegment(sketch, "E168", {"start": v(0, -67.43) * mm, "end": v(0, 65.55) * mm, "construction": true});
            skSolve(sketch);
        }
        {
            var Q0;
            Q0=makeQuery(id+"F9.opExtrude","SWEPT_BODY",BODY,{"disambiguationData":[OSD([sQuery(id+"F8.wireOp",EDGE,"E167")])]});
            var Q1;
            Q1=sQuery(id+"F10.wireOp",EDGE,"E168");
            circularPattern(context, id + "F11", {"operationType" : NewBodyOperationType.REMOVE, "entities" : qUnion([Q0]), "axis" : qUnion([Q1]), "angle" : 360 * degree, "instanceCount" : 3, "equalSpace" : true});
        }
        {
            var Q0;
            Q0=makeQuery(id+"F1.opExtrude","SWEPT_FACE",FACE,{"disambiguationData":[OSD([sQuery(id+"F0.wireOp",EDGE,"E93")])]});
            var sketch = newSketch(context, id + "F12", { "sketchPlane" : qUnion([Q0])});
            skLineSegment(sketch, "E169", {"start": v(-17.98, 0) * mm, "end": v(-5.98, 0) * mm, "construction": true});
            skCircle(sketch, "E170", {"center": v(-11.98, 0) * mm, "radius": 3.9 * mm});
            skSolve(sketch);
        }
        {
            var Q0;
            Q0=makeQuery(id+"F12.imprint","IMPRINT",FACE,{"disambiguationData":[TD([[makeQuery(id+"F12.imprint","IMPRINT",EDGE,{"derivedFrom":sQuery(id+"F12.wireOp",EDGE,"E170")}),1.0]])]});
            extrude(context, id + "F13", {"entities" : qUnion([Q0]), "oppositeDirection" : true, "depth" : 18 * mm, "offsetDistance" : 25 * mm, "hasSecondDirection" : true, "secondDirectionOppositeDirection" : false, "secondDirectionDepth" : 1 * mm});
        }
        {
            var Q0;
            Q0=makeQuery(id+"F13.opExtrude","SWEPT_BODY",BODY,{"disambiguationData":[OSD([sQuery(id+"F12.wireOp",EDGE,"E170")])]});
            var Q1;
            Q1=sQuery(id+"F10.wireOp",EDGE,"E168");
            circularPattern(context, id + "F14", {"operationType" : NewBodyOperationType.REMOVE, "entities" : qUnion([Q0]), "axis" : qUnion([Q1]), "angle" : 360 * degree, "instanceCount" : 3, "equalSpace" : true});
        }
        {
            var Q0;
            Q0=makeQuery(id+"F1.opExtrude","SWEPT_FACE",FACE,{"disambiguationData":[OSD([sQuery(id+"F0.wireOp",EDGE,"E110")])]});
            var sketch = newSketch(context, id + "F15", { "sketchPlane" : qUnion([Q0])});
            skLineSegment(sketch, "E171", {"start": v(-12.3, 0) * mm, "end": v(-0.26, 0) * mm, "construction": true});
            skCircle(sketch, "E172", {"center": v(-6.27, 0) * mm, "radius": 3.9 * mm});
            skSolve(sketch);
        }
        {
            var Q0;
            Q0=makeQuery(id+"F15.imprint","IMPRINT",FACE,{"disambiguationData":[TD([[makeQuery(id+"F15.imprint","IMPRINT",EDGE,{"derivedFrom":sQuery(id+"F15.wireOp",EDGE,"E172")}),1.0]])]});
            extrude(context, id + "F16", {"entities" : qUnion([Q0]), "oppositeDirection" : true, "depth" : 18 * mm, "offsetDistance" : 25 * mm, "hasSecondDirection" : true, "secondDirectionOppositeDirection" : false, "secondDirectionDepth" : 1 * mm});
        }
        {
            var Q0;
            Q0=makeQuery(id+"F16.opExtrude","SWEPT_BODY",BODY,{"disambiguationData":[OSD([sQuery(id+"F15.wireOp",EDGE,"E172")])]});
            var Q1;
            Q1=sQuery(id+"F10.wireOp",EDGE,"E168");
            circularPattern(context, id + "F17", {"operationType" : NewBodyOperationType.REMOVE, "entities" : qUnion([Q0]), "axis" : qUnion([Q1]), "angle" : 360 * degree, "instanceCount" : 3, "equalSpace" : true});
        }
        {
            var Q0;
            Q0=makeQuery(id+"F11.boolean.opBoolean","INTERSECT",EDGE,{"derivedFrom":[makeQuery(id+"F1.opExtrude","SWEPT_FACE",FACE,{"disambiguationData":[OSD([sQuery(id+"F0.wireOp",EDGE,"E131")])]}),makeQuery(id+"F11.opPattern","COPY",FACE,{"derivedFrom":makeQuery(id+"F9.opExtrude","SWEPT_FACE",FACE,{"disambiguationData":[OSD([sQuery(id+"F8.wireOp",EDGE,"E167")])]}),"instanceName":"1"})]});
            var Q1;
            Q1=makeQuery(id+"F14.boolean.opBoolean","INTERSECT",EDGE,{"derivedFrom":[makeQuery(id+"F1.opExtrude","SWEPT_FACE",FACE,{"disambiguationData":[OSD([sQuery(id+"F0.wireOp",EDGE,"E148")])]}),makeQuery(id+"F14.opPattern","COPY",FACE,{"derivedFrom":makeQuery(id+"F13.opExtrude","SWEPT_FACE",FACE,{"disambiguationData":[OSD([sQuery(id+"F12.wireOp",EDGE,"E170")])]}),"instanceName":"1"})]});
            var Q2;
            Q2=makeQuery(id+"F17.boolean.opBoolean","INTERSECT",EDGE,{"derivedFrom":[makeQuery(id+"F1.opExtrude","SWEPT_FACE",FACE,{"disambiguationData":[OSD([sQuery(id+"F0.wireOp",EDGE,"E0")])]}),makeQuery(id+"F17.opPattern","COPY",FACE,{"derivedFrom":makeQuery(id+"F16.opExtrude","SWEPT_FACE",FACE,{"disambiguationData":[OSD([sQuery(id+"F15.wireOp",EDGE,"E172")])]}),"instanceName":"1"})]});
            var Q3;
            Q3=makeQuery(id+"F11.boolean.opBoolean","INTERSECT",EDGE,{"derivedFrom":[makeQuery(id+"F1.opExtrude","SWEPT_FACE",FACE,{"disambiguationData":[OSD([sQuery(id+"F0.wireOp",EDGE,"E21")])]}),makeQuery(id+"F11.opPattern","COPY",FACE,{"derivedFrom":makeQuery(id+"F9.opExtrude","SWEPT_FACE",FACE,{"disambiguationData":[OSD([sQuery(id+"F8.wireOp",EDGE,"E167")])]}),"instanceName":"2"})]});
            var Q4;
            Q4=makeQuery(id+"F14.boolean.opBoolean","INTERSECT",EDGE,{"derivedFrom":[makeQuery(id+"F1.opExtrude","SWEPT_FACE",FACE,{"disambiguationData":[OSD([sQuery(id+"F0.wireOp",EDGE,"E38")])]}),makeQuery(id+"F14.opPattern","COPY",FACE,{"derivedFrom":makeQuery(id+"F13.opExtrude","SWEPT_FACE",FACE,{"disambiguationData":[OSD([sQuery(id+"F12.wireOp",EDGE,"E170")])]}),"instanceName":"2"})]});
            var Q5;
            Q5=makeQuery(id+"F17.boolean.opBoolean","INTERSECT",EDGE,{"derivedFrom":[makeQuery(id+"F1.opExtrude","SWEPT_FACE",FACE,{"disambiguationData":[OSD([sQuery(id+"F0.wireOp",EDGE,"E55")])]}),makeQuery(id+"F17.opPattern","COPY",FACE,{"derivedFrom":makeQuery(id+"F16.opExtrude","SWEPT_FACE",FACE,{"disambiguationData":[OSD([sQuery(id+"F15.wireOp",EDGE,"E172")])]}),"instanceName":"2"})]});
            var Q6;
            Q6=makeQuery(id+"F11.boolean.opBoolean","INTERSECT",EDGE,{"derivedFrom":[makeQuery(id+"F1.opExtrude","SWEPT_FACE",FACE,{"disambiguationData":[OSD([sQuery(id+"F0.wireOp",EDGE,"E76")])]}),makeQuery(id+"F9.opExtrude","SWEPT_FACE",FACE,{"disambiguationData":[OSD([sQuery(id+"F8.wireOp",EDGE,"E167")])]})]});
            var Q7;
            Q7=makeQuery(id+"F14.boolean.opBoolean","INTERSECT",EDGE,{"derivedFrom":[makeQuery(id+"F1.opExtrude","SWEPT_FACE",FACE,{"disambiguationData":[OSD([sQuery(id+"F0.wireOp",EDGE,"E93")])]}),makeQuery(id+"F13.opExtrude","SWEPT_FACE",FACE,{"disambiguationData":[OSD([sQuery(id+"F12.wireOp",EDGE,"E170")])]})]});
            var Q8;
            Q8=makeQuery(id+"F17.boolean.opBoolean","INTERSECT",EDGE,{"derivedFrom":[makeQuery(id+"F1.opExtrude","SWEPT_FACE",FACE,{"disambiguationData":[OSD([sQuery(id+"F0.wireOp",EDGE,"E110")])]}),makeQuery(id+"F16.opExtrude","SWEPT_FACE",FACE,{"disambiguationData":[OSD([sQuery(id+"F15.wireOp",EDGE,"E172")])]})]});
            chamfer(context, id + "F18", {"entities" : qUnion([Q0, Q1, Q2, Q3, Q4, Q5, Q6, Q7, Q8]), "width" : 0.5 * mm, "tangentPropagation" : true});
        }
    });
